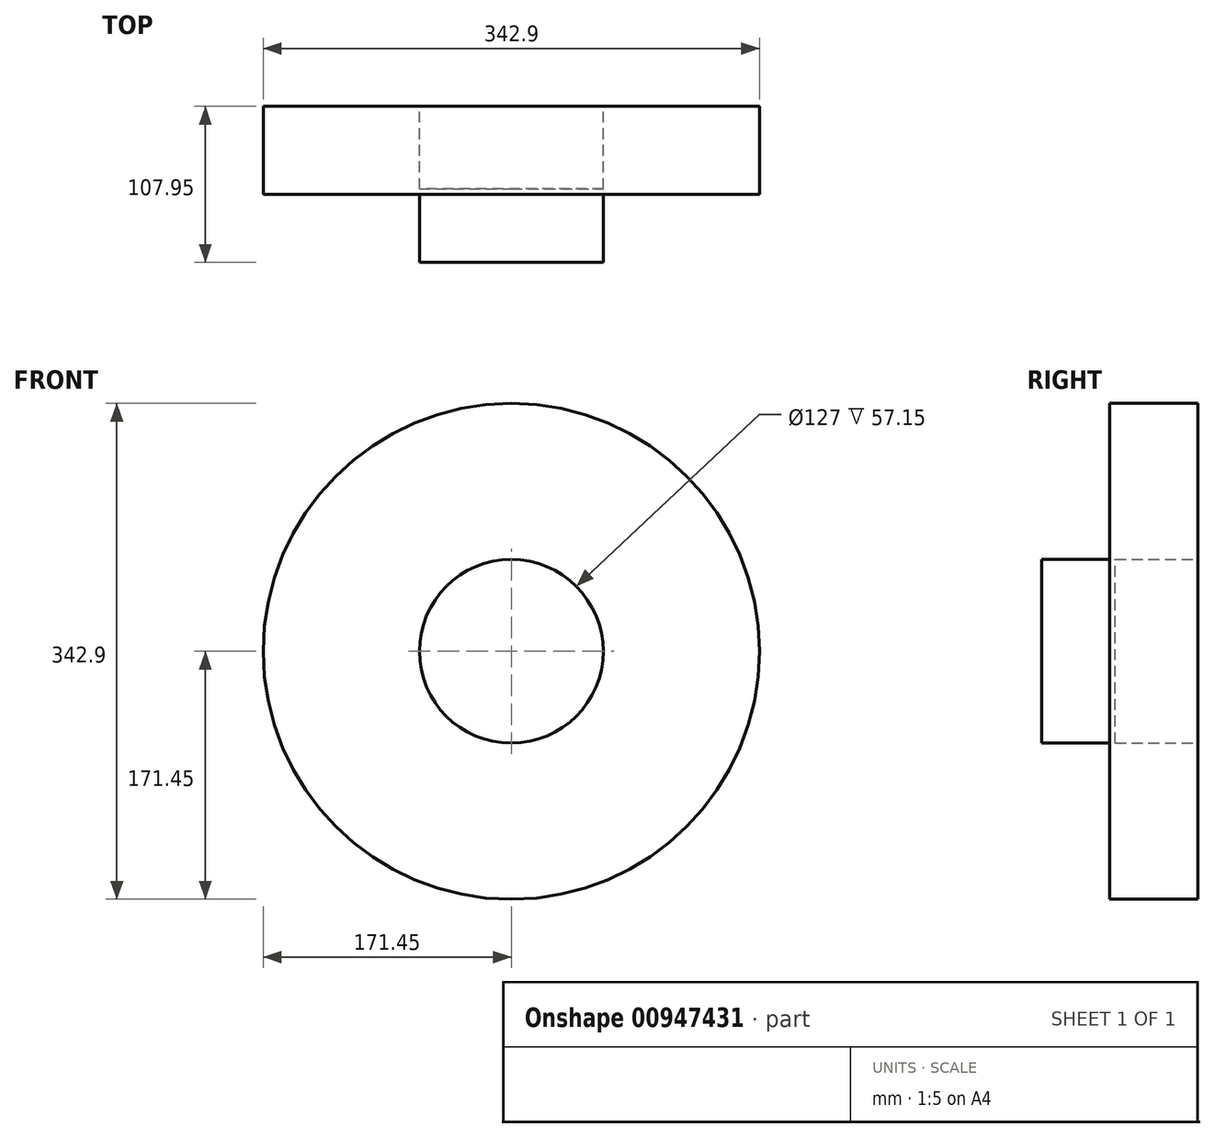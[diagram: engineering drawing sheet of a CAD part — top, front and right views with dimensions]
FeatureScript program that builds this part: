
annotation { "Feature Type Name" : "Feature", "Feature Type Description" : "" }
export const myFeature = defineFeature(function(context is Context, id is Id, definition is map)
    precondition{}
    {
        {
            var Q0;
            Q0=qCreatedBy(makeId("Front.planeOp"),FACE);
            var sketch = newSketch(context, id + "F0", { "sketchPlane" : qUnion([Q0])});
            skCircle(sketch, "E0", {"center": v(0, 0) * mm, "radius": 63.5 * mm});
            skCircle(sketch, "E1", {"center": v(0, 0) * mm, "radius": 171.45 * mm});
            skPoint(sketch, "E2", {"position": v(-228.6, 0) * mm});
            skPoint(sketch, "E3", {"position": v(0, -209.55) * mm});
            skPoint(sketch, "E4", {"position": v(190.5, 0) * mm});
            skPoint(sketch, "E5", {"position": v(0, 171.45) * mm});
            skPoint(sketch, "E6", {"position": v(141.44, -141.44) * mm});
            skPoint(sketch, "E7", {"position": v(-154.9, -154.9) * mm});
            skPoint(sketch, "E8", {"position": v(-228.6, 222.25) * mm});
            skPoint(sketch, "E9", {"position": v(127.97, 127.97) * mm});
            skLineSegment(sketch, "E10", {"start": v(0, 0) * mm, "end": v(127.97, 127.97) * mm, "construction": true});
            skLineSegment(sketch, "E11", {"start": v(141.44, -141.44) * mm, "end": v(0, 0) * mm, "construction": true});
            skLineSegment(sketch, "E12", {"start": v(0, 0) * mm, "end": v(-154.9, -154.9) * mm, "construction": true});
            skLineSegment(sketch, "E13", {"start": v(-487.08, 0) * mm, "end": v(487.08, 0) * mm, "construction": true});
            skLineSegment(sketch, "E14", {"start": v(-228.6, 0) * mm, "end": v(-228.6, 222.25) * mm});
            skLineSegment(sketch, "E15", {"start": v(190.5, 209.55) * mm, "end": v(190.5, 0) * mm, "construction": true});
            skLineSegment(sketch, "E16", {"start": v(209.55, -209.55) * mm, "end": v(0, -209.55) * mm, "construction": true});
            skLineSegment(sketch, "E17", {"start": v(-228.6, 0) * mm, "end": v(-228.6, -209.55) * mm, "construction": true});
            skArc(sketch, "E18", {"start": v(190.5, 0) * mm, "mid": v(128.15, 122.28) * mm, "end": v(0, 171.45) * mm});
            skArc(sketch, "E19", {"start": v(0, -209.55) * mm, "mid": v(135.76, -141.6) * mm, "end": v(190.5, 0) * mm});
            skArc(sketch, "E20", {"start": v(-228.6, 0) * mm, "mid": v(-155.06, -149.24) * mm, "end": v(0, -209.55) * mm});
            skLineSegment(sketch, "E21", {"start": v(-228.6, 222.25) * mm, "end": v(-69.85, 222.25) * mm});
            skLineSegment(sketch, "E22", {"start": v(-69.85, 222.25) * mm, "end": v(-69.85, 196.85) * mm});
            skLineSegment(sketch, "E23", {"start": v(-44.45, 171.45) * mm, "end": v(0, 171.45) * mm});
            skPoint(sketch, "E24.visualSharp", {"position": v(-69.85, 171.45) * mm});
            skArc(sketch, "E24.filletArc", {"start": v(-69.85, 196.85) * mm, "mid": v(-62.41, 178.89) * mm, "end": v(-44.45, 171.45) * mm});
            skLineSegment(sketch, "E25", {"start": v(-228.6, 222.25) * mm, "end": v(-250.83, 222.25) * mm});
            skLineSegment(sketch, "E26", {"start": v(-250.83, 222.25) * mm, "end": v(-250.83, 241.3) * mm});
            skLineSegment(sketch, "E27", {"start": v(-250.83, 241.3) * mm, "end": v(-47.63, 241.3) * mm});
            skLineSegment(sketch, "E28", {"start": v(-47.63, 241.3) * mm, "end": v(-47.63, 222.25) * mm});
            skLineSegment(sketch, "E29", {"start": v(-47.63, 222.25) * mm, "end": v(-69.85, 222.25) * mm});
            skPoint(sketch, "E30", {"position": v(0, 63.5) * mm});
            skPoint(sketch, "E31", {"position": v(0, -63.5) * mm});
            skSolve(sketch);
        }
        {
            var Q0;
            Q0=qCreatedBy(makeId("Right.planeOp"),FACE);
            var sketch = newSketch(context, id + "F1", { "sketchPlane" : qUnion([Q0])});
            skLineSegment(sketch, "E32.bottom", {"start": v(-57.15, -209.55) * mm, "end": v(57.15, -209.55) * mm});
            skLineSegment(sketch, "E32.top", {"start": v(-57.15, 222.25) * mm, "end": v(57.15, 222.25) * mm});
            skLineSegment(sketch, "E32.left", {"start": v(-57.15, -209.55) * mm, "end": v(-57.15, 222.25) * mm});
            skLineSegment(sketch, "E32.right", {"start": v(57.15, -209.55) * mm, "end": v(57.15, 222.25) * mm});
            skLineSegment(sketch, "E33", {"start": v(-57.15, 222.25) * mm, "end": v(-82.55, 222.25) * mm});
            skLineSegment(sketch, "E34", {"start": v(-82.55, 222.25) * mm, "end": v(-82.55, 241.3) * mm});
            skLineSegment(sketch, "E35", {"start": v(-82.55, 241.3) * mm, "end": v(82.55, 241.3) * mm});
            skLineSegment(sketch, "E36", {"start": v(82.55, 241.3) * mm, "end": v(82.55, 222.25) * mm});
            skLineSegment(sketch, "E37", {"start": v(82.55, 222.25) * mm, "end": v(57.15, 222.25) * mm});
            skLineSegment(sketch, "E38", {"start": v(-57.15, 63.5) * mm, "end": v(-107.95, 63.5) * mm});
            skLineSegment(sketch, "E39", {"start": v(-107.95, 63.5) * mm, "end": v(-107.95, -63.5) * mm});
            skLineSegment(sketch, "E40", {"start": v(-107.95, -63.5) * mm, "end": v(-57.15, -63.5) * mm});
            skSolve(sketch);
        }
        {
            var Q0;
            Q0=makeQuery(id+"F0.imprint","IMPRINT",FACE,{"disambiguationData":[TD([[makeQuery(id+"F0.imprint","IMPRINT",EDGE,{"derivedFrom":sQuery(id+"F0.wireOp",EDGE,"E21")}),1.0]])]});
            var Q1;
            Q1=makeQuery(id+"F0.imprint","IMPRINT",FACE,{"disambiguationData":[TD([[makeQuery(id+"F0.imprint","IMPRINT",EDGE,{"derivedFrom":sQuery(id+"F0.wireOp",EDGE,"E1")}),-1.0]])]});
            var Q2;
            Q2=makeQuery(id+"F0.imprint","IMPRINT",FACE,{"disambiguationData":[TD([[makeQuery(id+"F0.imprint","IMPRINT",EDGE,{"derivedFrom":sQuery(id+"F0.wireOp",EDGE,"E0")}),-1.0]])]});
            var Q3;
            Q3=makeQuery(id+"F0.imprint","IMPRINT",FACE,{"disambiguationData":[TD([[makeQuery(id+"F0.imprint","IMPRINT",EDGE,{"derivedFrom":sQuery(id+"F0.wireOp",EDGE,"E0")}),1.0]])]});
            extrude(context, id + "F2", {"entities" : qUnion([Q0, Q1, Q2, Q3]), "endBound" : BoundingType.SYMMETRIC, "depth" : 2540 * mm, "offsetDistance" : 25.4 * mm});
        }
        {
            var Q0;
            Q0=makeQuery(id+"F1.imprint","IMPRINT",FACE,{"disambiguationData":[TD([[makeQuery(id+"F1.imprint","IMPRINT",EDGE,{"derivedFrom":sQuery(id+"F1.wireOp",EDGE,"E32.top")}),1.0]])]});
            var Q1;
            {var subQ3=sQuery(id+"F1.wireOp",EDGE,"E32.bottom");Q1=makeQuery(id+"F1.imprint","IMPRINT",FACE,{"disambiguationData":[TD([[makeQuery(id+"F1.imprint","IMPRINT",EDGE,{"derivedFrom":subQ3}),1.0]])]});}
            extrude(context, id + "F3", {"entities" : qUnion([Q0, Q1]), "operationType" : NewBodyOperationType.INTERSECT, "endBound" : BoundingType.SYMMETRIC, "depth" : 2540 * mm, "offsetDistance" : 25.4 * mm});
        }
        {
            var Q0;
            Q0=makeQuery(id+"F0.imprint","IMPRINT",FACE,{"disambiguationData":[TD([[makeQuery(id+"F0.imprint","IMPRINT",EDGE,{"derivedFrom":sQuery(id+"F0.wireOp",EDGE,"E0")}),1.0]])]});
            extrude(context, id + "F4", {"entities" : qUnion([Q0]), "endBound" : BoundingType.SYMMETRIC, "depth" : 2540 * mm, "offsetDistance" : 25.4 * mm});
        }
        {
            var Q0;
            {var subQ0=sQuery(id+"F1.wireOp",EDGE,"E38");Q0=makeQuery(id+"F1.imprint","IMPRINT",FACE,{"disambiguationData":[TD([[makeQuery(id+"F1.imprint","IMPRINT",EDGE,{"derivedFrom":subQ0}),1.0]])]});}
            extrude(context, id + "F5", {"entities" : qUnion([Q0]), "operationType" : NewBodyOperationType.INTERSECT, "endBound" : BoundingType.SYMMETRIC, "depth" : 2540 * mm, "offsetDistance" : 25.4 * mm});
        }
        {
            var Q0;
            Q0=makeQuery(id+"F0.imprint","IMPRINT",FACE,{"disambiguationData":[TD([[makeQuery(id+"F0.imprint","IMPRINT",EDGE,{"derivedFrom":sQuery(id+"F0.wireOp",EDGE,"E0")}),-1.0]])]});
            extrude(context, id + "F6", {"entities" : qUnion([Q0]), "operationType" : NewBodyOperationType.ADD, "depth" : 60.96 * mm, "offsetDistance" : 25.4 * mm});
        }
    });
